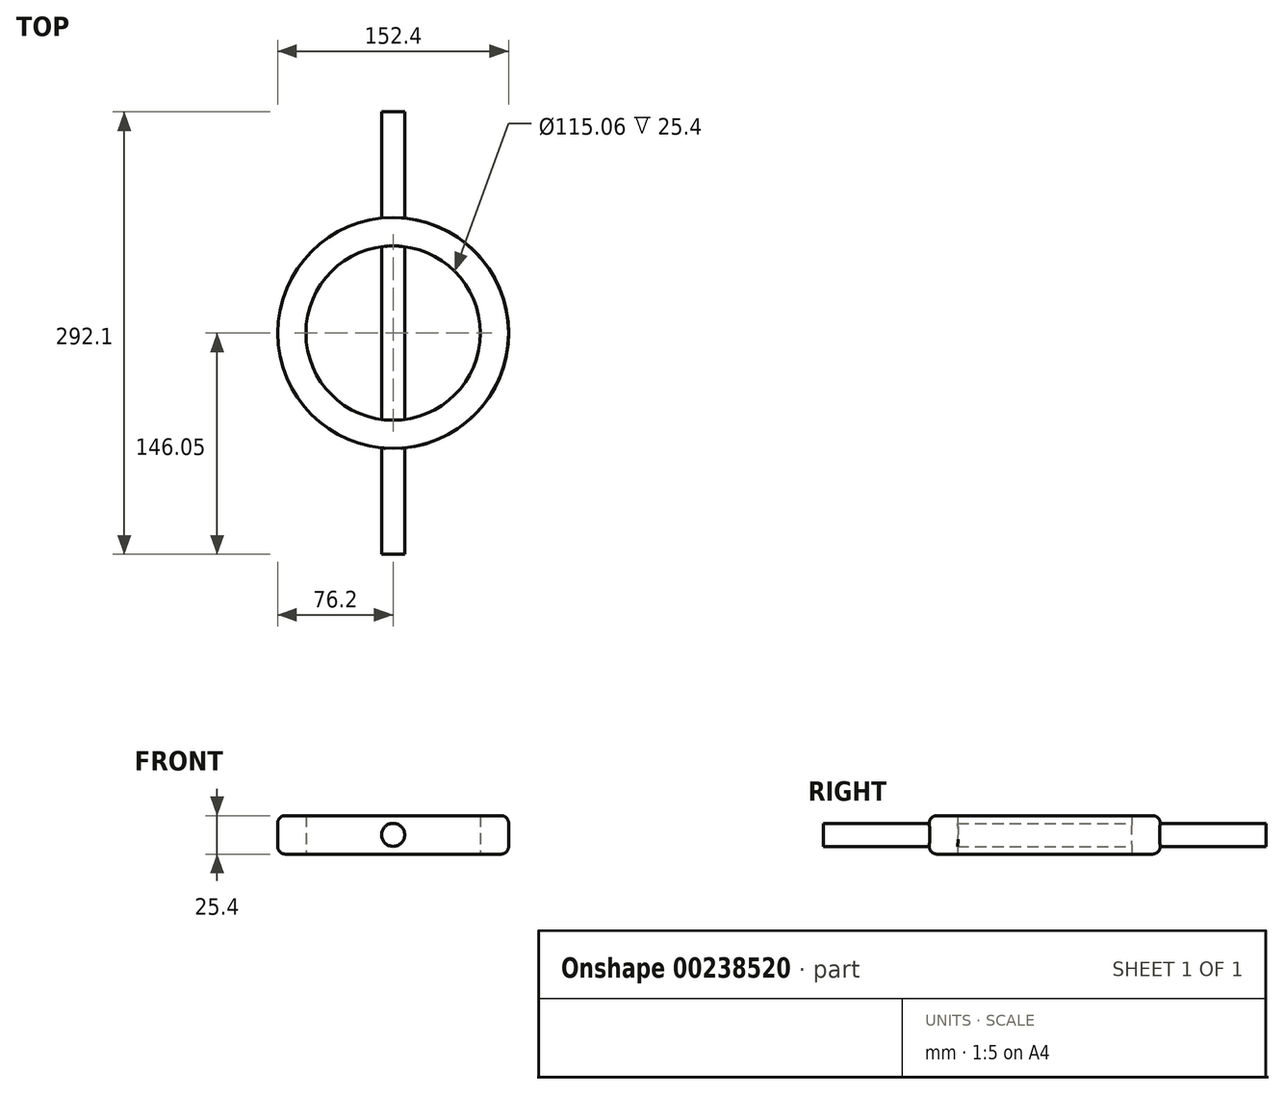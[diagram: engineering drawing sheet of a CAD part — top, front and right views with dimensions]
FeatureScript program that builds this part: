
annotation { "Feature Type Name" : "Feature", "Feature Type Description" : "" }
export const myFeature = defineFeature(function(context is Context, id is Id, definition is map)
    precondition{}
    {
        {
            var Q0;
            Q0=qCreatedBy(makeId("Top.planeOp"),FACE);
            var sketch = newSketch(context, id + "F0", { "sketchPlane" : qUnion([Q0])});
            skCircle(sketch, "E0", {"center": v(0, 0) * mm, "radius": 76.2 * mm});
            skCircle(sketch, "E1", {"center": v(0, 0) * mm, "radius": 57.53 * mm});
            skSolve(sketch);
        }
        {
            var Q0;
            Q0=makeQuery(id+"F0.imprint","IMPRINT",FACE,{"disambiguationData":[TD([[makeQuery(id+"F0.imprint","IMPRINT",EDGE,{"derivedFrom":sQuery(id+"F0.wireOp",EDGE,"E0")}),1.0]])]});
            extrude(context, id + "F1", {"entities" : qUnion([Q0]), "depth" : 25.4 * mm});
        }
        {
            var Q0;
            Q0=makeQuery(id+"F1.opExtrude","CAP_EDGE",EDGE,{"disambiguationData":[OSD([sQuery(id+"F0.wireOp",EDGE,"E0")])],"isStart":false});
            var Q1;
            Q1=makeQuery(id+"F1.opExtrude","CAP_EDGE",EDGE,{"disambiguationData":[OSD([sQuery(id+"F0.wireOp",EDGE,"E0")])],"isStart":true});
            fillet(context, id + "F2", {"entities" : qUnion([Q0, Q1]), "radius" : 5.08 * mm, "tangentPropagation" : true, "allowEdgeOverflow" : false});
        }
        {
            var Q0;
            Q0=qCreatedBy(makeId("Front.planeOp"),FACE);
            var sketch = newSketch(context, id + "F3", { "sketchPlane" : qUnion([Q0])});
            skCircle(sketch, "E2", {"center": v(0, 12.7) * mm, "radius": 7.62 * mm});
            skSolve(sketch);
        }
        {
            var Q0;
            Q0=makeQuery(id+"F3.imprint","IMPRINT",FACE,{"disambiguationData":[TD([[makeQuery(id+"F3.imprint","IMPRINT",EDGE,{"derivedFrom":sQuery(id+"F3.wireOp",EDGE,"E2")}),1.0]])]});
            extrude(context, id + "F4", {"entities" : qUnion([Q0]), "depth" : 146.05 * mm});
        }
        {
            var Q0;
            Q0=makeQuery(id+"F4.opExtrude","CAP_FACE",FACE,{"disambiguationData":[OSD([sQuery(id+"F3.wireOp",EDGE,"E2")])],"isStart":true});
            extrude(context, id + "F5", {"entities" : qUnion([Q0]), "operationType" : NewBodyOperationType.ADD, "depth" : 146.05 * mm});
        }
    });
